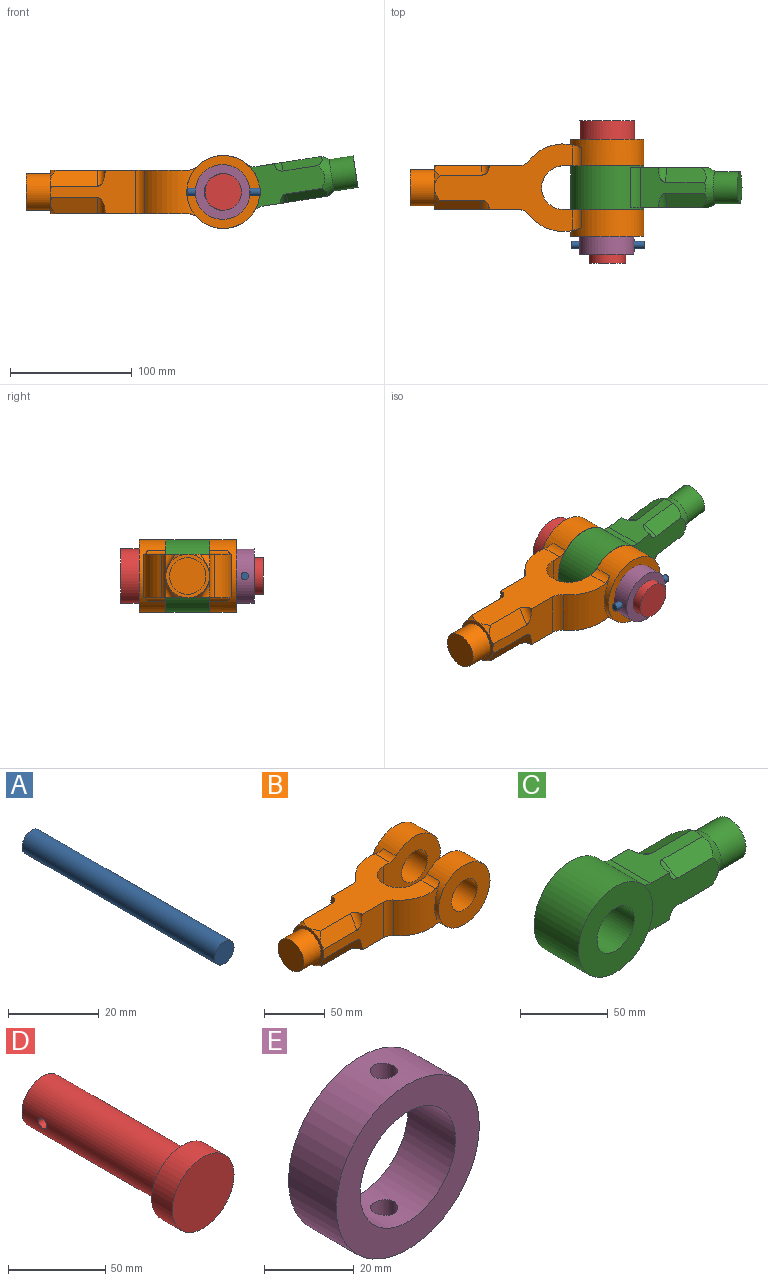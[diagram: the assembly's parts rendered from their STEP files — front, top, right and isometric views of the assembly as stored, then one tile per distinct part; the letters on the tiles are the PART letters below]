
ASSEMBLY  parts=5 mates=4
PART A: 3 faces, bbox 6x60x6 mm
  f0: cylinder r=3mm len=60mm, axis (0,1,0), area 1131mm2, adj f1,f2
  f1: plane 6x6mm, normal (0,-1,0), area 28.3mm2, adj f0
  f2: plane 6x6mm, normal (0,1,0), area 28.3mm2, adj f0
PART B: 44 faces, bbox 192.2x80x60 mm
  f0: plane 39.01x13.18mm, normal (0,-0.87,-0.5), area 574.4mm2, adj f1,f6,f22,f26,f34
  f1: cone r=13.45mm half-angle=30deg, axis (1,0,0), area 4mm2, adj f0,f22,f31
  f2: cone r=13.45mm half-angle=30deg, axis (1,0,0), area 4mm2, adj f7,f22,f31
  f3: plane 39.01x13.18mm, normal (0,0.87,0.5), area 574.4mm2, adj f5,f25,f28,f29,f35
  f4: cone r=13.45mm half-angle=30deg, axis (1,0,0), area 4mm2, adj f8,f25,f31
  f5: plane 113.62x72mm, normal (0,0,1), area 3680mm2, adj f3,f7,f9,f10,f16,f17,f21,f22
  f6: plane 113.62x72mm, normal (0,0,-1), area 3680mm2, adj f0,f8,f11,f12,f16,f17,f21,f22
  f7: plane 39.01x13.18mm, normal (0,-0.87,0.5), area 574.4mm2, adj f2,f5,f22,f30,f37
  f8: plane 39.01x13.18mm, normal (0,0.87,-0.5), area 574.4mm2, adj f4,f6,f25,f27,f36
  f9: plane 1.18x0.68mm, normal (-1,0,0), area 0.4mm2, adj f5,f22,f37
  f10: plane 1.18x0.68mm, normal (-1,0,0), area 0.4mm2, adj f5,f25,f35
  f11: plane 1.18x0.68mm, normal (-1,0,0), area 0.4mm2, adj f6,f25,f36
  f12: plane 1.18x0.68mm, normal (-1,0,0), area 0.4mm2, adj f6,f22,f34
  f13: cylinder r=15mm len=30mm, axis (0,1,0), area 2073.5mm2, adj f15,f16
  f14: cylinder r=30mm len=60mm, axis (0,1,0), area 3366.4mm2, adj f15,f16,f17,f40,f41
  f15: plane 60x60mm, normal (0,-1,0), area 2120.6mm2, adj f13,f14
  f16: plane 66x60mm, normal (0,1,0), area 2410.7mm2, adj f5,f6,f13,f14,f23,f40,f41
  f17: cylinder r=36mm len=43.14mm, axis (0,0,-1), area 1480.7mm2, adj f5,f6,f14,f39,f40,f41
  f18: cylinder r=15mm len=30mm, axis (0,-1,0), area 2073.5mm2, adj f20,f21
  f19: cylinder r=30mm len=60mm, axis (0,-1,0), area 3366.5mm2, adj f20,f21,f24,f42,f43
  f20: plane 60x60mm, normal (0,1,0), area 2120.6mm2, adj f18,f19
  f21: plane 66x60mm, normal (0,-1,0), area 2410.7mm2, adj f5,f6,f18,f19,f23,f42,f43
  f22: plane 69.69x36mm, normal (0,-1,0), area 1349.9mm2, adj f0,f1,f2,f5,f6,f7,f9,f12
  f23: cylinder r=18mm len=36mm, axis (0,0,-1), area 2035.8mm2, adj f5,f6,f16,f21
  f24: cylinder r=36mm len=43.14mm, axis (0,0,-1), area 1480.7mm2, adj f5,f6,f19,f38,f42,f43
  f25: plane 69.69x36mm, normal (0,1,0), area 1349.9mm2, adj f3,f4,f5,f6,f8,f10,f11,f28
  f26: cone r=13.45mm half-angle=30deg, axis (1,0,0), area 34.8mm2, adj f0,f6,f31
  f27: cone r=13.45mm half-angle=30deg, axis (1,0,0), area 34.8mm2, adj f6,f8,f31
  f28: cone r=13.45mm half-angle=30deg, axis (1,0,0), area 4mm2, adj f3,f25,f31
  f29: cone r=13.45mm half-angle=30deg, axis (1,0,0), area 34.8mm2, adj f3,f5,f31
  f30: cone r=13.45mm half-angle=30deg, axis (1,0,0), area 34.8mm2, adj f5,f7,f31
  f31: plane 36x36mm, normal (-1,0,0), area 310mm2, adj f1,f2,f4,f26,f27,f28,f29,f30
  f32: cylinder r=15.01mm len=30.02mm, axis (1,0,0), area 1886.4mm2, adj f31,f33
  f33: plane 30.02x30.02mm, normal (-1,0,0), area 707.9mm2, adj f32
  f34: cylinder r=6mm len=16.18mm, axis (0,0.5,-0.87), area 95.9mm2, adj f0,f6,f12,f22
  f35: cylinder r=6mm len=16.18mm, axis (0,-0.5,0.87), area 95.9mm2, adj f3,f5,f10,f25
  f36: cylinder r=6mm len=16.18mm, axis (0,0.5,0.87), area 95.9mm2, adj f6,f8,f11,f25
  f37: cylinder r=6mm len=16.18mm, axis (0,-0.5,-0.87), area 95.9mm2, adj f5,f7,f9,f22
  f38: cylinder r=10mm len=36mm, axis (0,0,-1), area 329.9mm2, adj f5,f6,f24,f25
  f39: cylinder r=10mm len=36mm, axis (0,0,-1), area 329.9mm2, adj f5,f6,f17,f22
  f40: cylinder r=10mm len=17.22mm, axis (0,1,0), area 128.4mm2, adj f5,f14,f16,f17
  f41: cylinder r=10mm len=17.22mm, axis (0,1,0), area 128.4mm2, adj f6,f14,f16,f17
  f42: cylinder r=10mm len=17.22mm, axis (0,-1,0), area 128.4mm2, adj f5,f19,f21,f24
  f43: cylinder r=10mm len=17.22mm, axis (0,-1,0), area 128.4mm2, adj f6,f19,f21,f24
PART C: 25 faces, bbox 140x39x60 mm
  f0: plane 33.43x12.09mm, normal (0,0.5,-0.87), area 450.2mm2, adj f2,f12,f14,f19
  f1: plane 33.43x12.09mm, normal (0,-0.5,0.87), area 450.2mm2, adj f2,f11,f13,f20
  f2: cone r=19.05mm half-angle=30deg, axis (-1,0,0), area 733.1mm2, adj f0,f1,f11,f12,f13,f14,f15,f16
  f3: plane 0.08x0.05mm, normal (1,0,0), area 0mm2, adj f11,f14,f17
  f4: plane 0.08x0.05mm, normal (1,0,0), area 0mm2, adj f12,f14,f19
  f5: plane 0.08x0.05mm, normal (1,0,0), area 0mm2, adj f12,f13,f18
  f6: plane 0.08x0.05mm, normal (1,0,0), area 0mm2, adj f11,f13,f20
  f7: cylinder r=15mm len=36mm, axis (0,-1,0), area 3392.9mm2, adj f9,f10
  f8: cylinder r=30mm len=60mm, axis (0,-1,0), area 5352mm2, adj f9,f10,f13,f14,f23,f24
  f9: plane 60x60mm, normal (0,1,0), area 2120.6mm2, adj f7,f8
  f10: plane 60x60mm, normal (0,-1,0), area 2120.6mm2, adj f7,f8
  f11: plane 54.46x33mm, normal (0,0,1), area 872.7mm2, adj f1,f2,f3,f6,f13,f14,f15,f17
  f12: plane 54.46x33mm, normal (0,0,-1), area 872.7mm2, adj f0,f2,f4,f5,f13,f14,f16,f18
  f13: plane 61.96x39.75mm, normal (0,-1,0), area 1293.9mm2, adj f1,f2,f5,f6,f8,f11,f12,f16
  f14: plane 61.96x39.75mm, normal (0,1,0), area 1293.9mm2, adj f0,f2,f3,f4,f8,f11,f12,f15
  f15: plane 33.43x12.09mm, normal (0,0.5,0.87), area 450.2mm2, adj f2,f11,f14,f17
  f16: plane 33.43x12.09mm, normal (0,-0.5,-0.87), area 450.2mm2, adj f2,f12,f13,f18
  f17: cylinder r=6mm len=15.08mm, axis (0,-0.87,0.5), area 84mm2, adj f3,f11,f14,f15
  f18: cylinder r=6mm len=15.08mm, axis (0,0.87,-0.5), area 84mm2, adj f5,f12,f13,f16
  f19: cylinder r=6mm len=15.08mm, axis (0,0.87,0.5), area 84mm2, adj f0,f4,f12,f14
  f20: cylinder r=6mm len=15.08mm, axis (0,-0.87,-0.5), area 84mm2, adj f1,f6,f11,f13
  f21: cylinder r=13.28mm len=26.56mm, axis (-1,0,0), area 1668.7mm2, adj f2,f22
  f22: plane 26.56x26.56mm, normal (1,0,0), area 554mm2, adj f21
  f23: cylinder r=10mm len=33mm, axis (0,-1,0), area 279.4mm2, adj f8,f11,f13,f14
  f24: cylinder r=10mm len=33mm, axis (0,-1,0), area 279.4mm2, adj f8,f12,f13,f14
PART D: 6 faces, bbox 45x117x45 mm
  f0: cylinder r=15mm len=102mm, axis (0,1,0), area 9556.3mm2, adj f1,f4,f5
  f1: plane 30x30mm, normal (0,1,0), area 706.9mm2, adj f0
  f2: cylinder r=22.5mm len=45mm, axis (0,1,0), area 2120.6mm2, adj f3,f4
  f3: plane 45x45mm, normal (0,-1,0), area 1590.4mm2, adj f2
  f4: plane 45x45mm, normal (0,1,0), area 883.6mm2, adj f0,f2
  f5: cylinder r=3mm len=30mm, axis (1,0,0), area 559.8mm2, adj f0
PART E: 6 faces, bbox 45x15x45 mm
  f0: cylinder r=22.5mm len=45mm, axis (0,-1,0), area 2063.7mm2, adj f1,f2,f4,f5
  f1: plane 45x45mm, normal (0,1,0), area 883.6mm2, adj f0,f3
  f2: plane 45x45mm, normal (0,-1,0), area 883.6mm2, adj f0,f3
  f3: cylinder r=15mm len=30mm, axis (0,-1,0), area 1356.8mm2, adj f1,f2,f4,f5
  f4: cylinder r=3mm len=7.8mm, axis (0,0,1), area 142.3mm2, adj f0,f3
  f5: cylinder r=3mm len=7.8mm, axis (0,0,1), area 142.3mm2, adj f0,f3
PLACE A rot(axis=(0,0,1),90deg) t=(109.07,-88.51,-99.17)mm
PLACE B t=(108.69,-59.51,-99.17)mm fixed
PLACE C rot(axis=(0,-1,0),8.8deg) t=(108.69,-41.51,-99.17)mm
PLACE D rot(axis=(1,0,0),180deg) t=(108.69,-52.51,-99.17)mm
PLACE E rot(axis=(0.71,0,-0.71),180deg) t=(108.16,-81.01,-99.17)mm
MATE fastened D.f0 <-> B.f13  axis (0,-1,0) through (108.69,-1.51,-99.17)mm
MATE fastened E.f4 <-> D.f5  axis (-1,0,0) through (93.51,-88.51,-99.17)mm
MATE slider A.f0 <-> E.f4  axis (-1,0,0) through (109.07,-88.51,-99.17)mm
MATE revolute C.f7 <-> B.f13  axis (0,-1,0) through (108.69,-59.51,-99.17)mm
